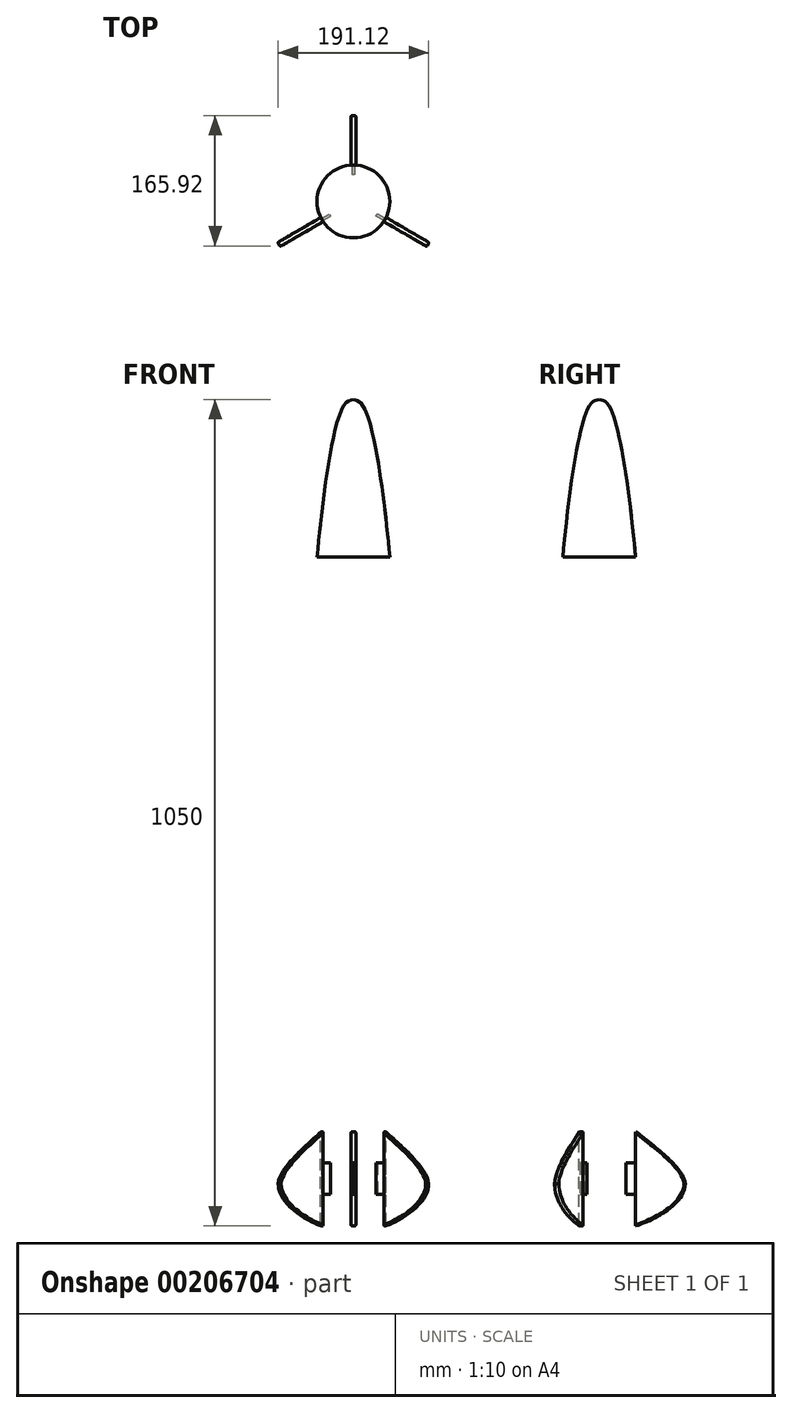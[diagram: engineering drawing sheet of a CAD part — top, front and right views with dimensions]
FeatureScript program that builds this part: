
annotation { "Feature Type Name" : "Feature", "Feature Type Description" : "" }
export const myFeature = defineFeature(function(context is Context, id is Id, definition is map)
    precondition{}
    {
        {
            assignVariable(context, id + "F0", {"name" : "thickness", "anyValue" : 0.7});
        }
        {
            var Q0;
            Q0=qCreatedBy(makeId("Front.planeOp"),FACE);
            var sketch = newSketch(context, id + "F1", { "sketchPlane" : qUnion([Q0])});
            skLineSegment(sketch, "E0", {"start": v(-46.25, 0) * mm, "end": v(0, 0) * mm});
            skLineSegment(sketch, "E1", {"start": v(0, 0) * mm, "end": v(0, 200) * mm});
            skFitSpline(sketch, "E2", {"points": [v(0, 200) * mm, v(-10.6, 194.67) * mm, v(-32.73, 112.09) * mm, v(-46.25, 0) * mm], "startDerivative": vector(-73.23, -11.85) * mm, "endDerivative": vector(-23.73, -238.66) * mm});
            skSolve(sketch);
        }
        {
            var Q0;
            Q0=makeQuery(id+"F1.imprint","IMPRINT",FACE,{"disambiguationData":[TD([[makeQuery(id+"F1.imprint","IMPRINT",EDGE,{"derivedFrom":sQuery(id+"F1.wireOp",EDGE,"E0")}),1.0]])]});
            var Q1;
            Q1=sQuery(id+"F1.wireOp",EDGE,"E1");
            revolve(context, id + "F2", {"entities" : qUnion([Q0]), "axis" : qUnion([Q1]), "revolveType" : RevolveType.FULL});
        }
        {
            var Q0;
            Q0=makeQuery(id+"F2.opRevolve","SWEPT_FACE",FACE,{"disambiguationData":[OSD([sQuery(id+"F1.wireOp",EDGE,"E0")])]});
            shell(context, id + "F3", {"entities" : qUnion([Q0]), "thickness" : (getVariable(context, 'thickness')) * mm});
        }
        {
            var Q0;
            Q0=qCreatedBy(makeId("Top.planeOp"),FACE);
            var sketch = newSketch(context, id + "F4", { "sketchPlane" : qUnion([Q0])});
            skCircle(sketch, "E3", {"center": v(0, 0) * mm, "radius": 46.25 * mm});
            skSolve(sketch);
        }
        {
            var Q0;
            Q0=sQuery(id+"F4.wireOp",EDGE,"E3");
            extrude(context, id + "F5", {"bodyType" : ToolBodyType.SURFACE, "surfaceEntities" : qUnion([Q0]), "oppositeDirection" : true, "depth" : 850 * mm});
        }
        {
            var Q0;
            Q0=qCreatedBy(makeId("Top.planeOp"),FACE);
            cPlane(context, id + "F6", {"entities" : qUnion([Q0]), "cplaneType" : CPlaneType.OFFSET, "offset" : 850 * mm, "oppositeDirection" : true, "width" : 150 * mm, "height" : 150 * mm});
        }
        {
            var Q0;
            Q0=qCreatedBy(makeId("Right.planeOp"),FACE);
            var sketch = newSketch(context, id + "F7", { "sketchPlane" : qUnion([Q0])});
            skLineSegment(sketch, "E4", {"start": v(46.25, -850) * mm, "end": v(46.25, -730) * mm});
            skLineSegment(sketch, "E5", {"start": v(109.25, -796.45) * mm, "end": v(109.25, -796.45) * mm});
            skFitSpline(sketch, "E6", {"points": [v(46.25, -730) * mm, v(109.25, -796.45) * mm], "startDerivative": vector(84.93, -66.5) * mm, "endDerivative": vector(3.02, -57.14) * mm});
            skFitSpline(sketch, "E7", {"points": [v(46.25, -850) * mm, v(109.25, -796.45) * mm], "startDerivative": vector(87, 29.19) * mm, "endDerivative": vector(1.56, 72.09) * mm});
            skSolve(sketch);
        }
        {
            var Q0;
            Q0=makeQuery(id+"F7.imprint","IMPRINT",FACE,{"disambiguationData":[TD([[makeQuery(id+"F7.imprint","IMPRINT",EDGE,{"derivedFrom":sQuery(id+"F7.wireOp",EDGE,"E4")}),-1.0]])]});
            extrude(context, id + "F8", {"entities" : qUnion([Q0]), "depth" : 3 * mm, "hasSecondDirection" : true, "secondDirectionOppositeDirection" : true, "secondDirectionDepth" : 3 * mm});
        }
        {
            var Q0;
            Q0=qCreatedBy(makeId("Right.planeOp"),FACE);
            var sketch = newSketch(context, id + "F9", { "sketchPlane" : qUnion([Q0])});
            skLineSegment(sketch, "E8", {"start": v(0, 0) * mm, "end": v(0, -873.85) * mm, "construction": true});
            skSolve(sketch);
        }
        {
            var Q0;
            Q0=qCreatedBy(makeId("Right.planeOp"),FACE);
            var sketch = newSketch(context, id + "F10", { "sketchPlane" : qUnion([Q0])});
            skLineSegment(sketch, "E9.bottom", {"start": v(46.25, -769.88) * mm, "end": v(34.25, -769.88) * mm});
            skLineSegment(sketch, "E9.top", {"start": v(46.25, -809.88) * mm, "end": v(34.25, -809.88) * mm});
            skLineSegment(sketch, "E9.left", {"start": v(46.25, -769.88) * mm, "end": v(46.25, -809.88) * mm});
            skLineSegment(sketch, "E9.right", {"start": v(34.25, -769.88) * mm, "end": v(34.25, -809.88) * mm});
            skSolve(sketch);
        }
        {
            var Q0;
            Q0=makeQuery(id+"F10.imprint","IMPRINT",FACE,{"disambiguationData":[TD([[makeQuery(id+"F10.imprint","IMPRINT",EDGE,{"derivedFrom":sQuery(id+"F10.wireOp",EDGE,"E9.bottom")}),1.0]])]});
            extrude(context, id + "F11", {"entities" : qUnion([Q0]), "depth" : 1.5 * mm, "hasSecondDirection" : true, "secondDirectionOppositeDirection" : true, "secondDirectionDepth" : 1.5 * mm});
        }
        {
            var Q0;
            Q0=makeQuery(id+"F8.opExtrude","CAP_EDGE",EDGE,{"disambiguationData":[OSD([sQuery(id+"F7.wireOp",EDGE,"E6")])],"isStart":true});
            var Q1;
            Q1=makeQuery(id+"F8.opExtrude","CAP_EDGE",EDGE,{"disambiguationData":[OSD([sQuery(id+"F7.wireOp",EDGE,"E7")])],"isStart":true});
            var Q2;
            Q2=makeQuery(id+"F8.opExtrude","CAP_EDGE",EDGE,{"disambiguationData":[OSD([sQuery(id+"F7.wireOp",EDGE,"E6")])],"isStart":false});
            var Q3;
            Q3=makeQuery(id+"F8.opExtrude","CAP_EDGE",EDGE,{"disambiguationData":[OSD([sQuery(id+"F7.wireOp",EDGE,"E7")])],"isStart":false});
            fillet(context, id + "F12", {"entities" : qUnion([Q0, Q1, Q2, Q3]), "radius" : 1.5 * mm, "tangentPropagation" : true, "allowEdgeOverflow" : false});
        }
        {
            var Q0;
            Q0=makeQuery(id+"F8.opExtrude","SWEPT_BODY",BODY,{"disambiguationData":[OSD([sQuery(id+"F7.wireOp",EDGE,"MLaW5EzB-dxzK-ol2A-ZuAM-jGAGmTGvtbjY"),sQuery(id+"F7.wireOp",EDGE,"j16giBFC-98s1-P62o-qHxt-FUimGxetoBhM"),sQuery(id+"F7.wireOp",EDGE,"p8N4ACxB-fmJU-W3xu-IbnH-ZCZMqmmzuwiT"),sQuery(id+"F7.wireOp",EDGE,"mTKjpFEP-VPrW-hY9o-Uc6Q-96XcXkIvoQyr"),sQuery(id+"F7.wireOp",EDGE,"E4"),sQuery(id+"F7.wireOp",EDGE,"E5"),sQuery(id+"F7.wireOp",EDGE,"E6"),sQuery(id+"F7.wireOp",EDGE,"E7")])]});
            var Q1;
            Q1=makeQuery(id+"F11.opExtrude","SWEPT_BODY",BODY,{"disambiguationData":[OSD([sQuery(id+"F10.wireOp",EDGE,"E9.bottom"),sQuery(id+"F10.wireOp",EDGE,"E9.top"),sQuery(id+"F10.wireOp",EDGE,"E9.left"),sQuery(id+"F10.wireOp",EDGE,"E9.right")])]});
            var Q2;
            Q2=sQuery(id+"F9.wireOp",EDGE,"E8");
            circularPattern(context, id + "F13", {"entities" : qUnion([Q0, Q1]), "axis" : qUnion([Q2]), "angle" : 360 * degree, "instanceCount" : 3, "equalSpace" : true});
        }
    });
